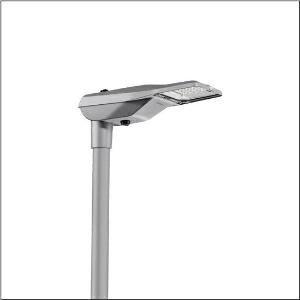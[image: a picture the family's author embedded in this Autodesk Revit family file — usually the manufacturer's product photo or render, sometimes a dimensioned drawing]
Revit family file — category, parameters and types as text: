
# Revit family: streetlight_sl_21_micro___stw1_0a_5xe1e33t08db_9129
name_source: partatom
category: Lighting Fixtures
units: mm (PartAtom-declared; Revit-internal decimal feet)

## family parameters
Cut with Voids When Loaded = No
Host = Face
Light Source = No
Part Type = Normal
Room Calculation Point = No
Round Connector Dimension = Use Diameter
Shared = No

## types (1)
- --- (1 x LED, 5110 lm, 39.1 W, 3000K)
    Apparent Load = 39 VA
    CIE Flux Codes = 38 75 98 100 100
    Color Rendering = 70
    Color Temperature = 3000K
    Default Elevation = 1800 mm
    Description = Streetlight SL 21 micro, mast luminaire, primary light control with lens, of PMMA, primary optical cover: cover, of toughened safety glass, transparent, light distribution: STW1.0a, light emission: direct distribution, primary light characteristic: asymmetric, installation type: side-entry, post-top, LED, High Power LED, rated luminous flux: 5.110lm, luminous efficacy: 131lm/W, light colour: 730, colour temperature: 3000K, control: flexible luminous flux parameterisation, time-dependent luminous flux control, constant luminous flux control, overheat protection, presetting dimming logarithmic, mains connection: 220..240V, AC, 50/60Hz, start of lifetime: 39W, end of service life: 41W, reduction: 18W, luminaire housing, of diecast aluminium, powder-coated, Siteco® metallic grey (DB 702S), corrosivity category C5 mid according to DIN EN ISO 12944, please order mast flange separately, inclination adjustable: 0°, 5°, 10°, 15°, sealing non-destructively replaceable, multi-level sealing system, length: 528mm, width: 235mm, height: 110mm, mast flange for spigot size: 42mm (side-entry): 5XC10008XM4, 60/48mm (side-entry/post-top): 5XC10108XM2, 76/60mm (side-entry/post-top): 5XC10108XM1, Smart Interface below and above, protection rating (complete): IP66, insulation class (complete): insulation class II (safety insulation), certification: CE, ENEC, ENEC+, VDE, impact resistance: IK09, permissible operating ambient temperature for outdoor applications: -40..+50°C, standard-compliant lighting for roads and squares, packaging unit: 1 piece

Light Distribution: STW1.0a
    Height = 110 mm
    Lamp = 1 x LED
    Lamp Light Flux = 5110 lm
    Lamp Power = 39.1 W
    Lamp count = 1
    Length = 528 mm
    Luminous efficacy = 131 lm/W
    Manufacturer = Siteco
    ModVariant = No
    Model = 5XE1E33T08DB
    Number of Poles = 1
    OnlyDefault = Yes
    Power Factor = 1
    Product Name = Streetlight SL 21 micro | STW1.0a
    Product group = mast luminaire | pylon top
    ProductGroupID = 6100
    Protection Class = Protection class II
    Protection Degree = IP 66
    RLX_Detail_Level = 1
    RLX_Emergency_Light_Flux = 0 lm
    RLX_Emergency_Type = 0
    RLX_Emergency_Type_DB = No
    RlxData = <blob elided: 98493 chars, md5=95ccfff1>
    Socket = socket
    Standby Power = 0 W
    System Light Flux = 5110 lm
    System Power = 39 W
    Type Comments = factory setting: luminous flux: 100 % | dim-lin: 254 | 765 mA
    Type Image = l_1007239.jpg
    URL = http://relux.com
    VarID = @adj_105427
    Voltage = 0 V
    Weight = 0.00 kg
    Width = 235 mm

## geometry (parser evidence)
native form markers: Blend x4, Sweep x9
no freeform markers — native parametric forms only
